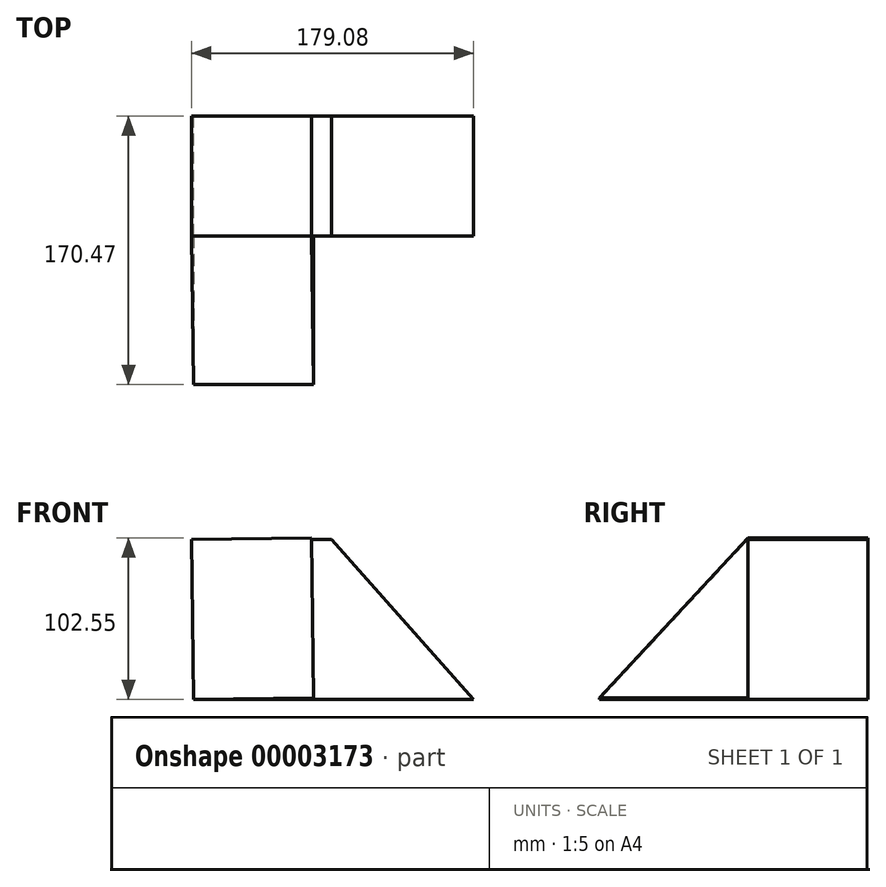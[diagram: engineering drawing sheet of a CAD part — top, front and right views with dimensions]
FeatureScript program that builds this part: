
annotation { "Feature Type Name" : "Feature", "Feature Type Description" : "" }
export const myFeature = defineFeature(function(context is Context, id is Id, definition is map)
    precondition{}
    {
        {
            var Q0;
            Q0=qCreatedBy(makeId("Front.planeOp"),FACE);
            var sketch = newSketch(context, id + "F0", { "sketchPlane" : qUnion([Q0])});
            skLineSegment(sketch, "E0.rect.bottom", {"start": v(-0.64, 50.8) * mm, "end": v(-89.54, 50.8) * mm});
            skLineSegment(sketch, "E0.rect.top", {"start": v(89.54, -50.8) * mm, "end": v(-88.26, -50.8) * mm});
            skLineSegment(sketch, "E0.rect.right", {"start": v(-89.54, 50.8) * mm, "end": v(-88.26, -50.8) * mm});
            skPoint(sketch, "E0.rect.middle", {"position": v(0, 0) * mm});
            skLineSegment(sketch, "E1", {"start": v(-0.64, 50.8) * mm, "end": v(89.54, -50.8) * mm});
            skPoint(sketch, "E2.orphan", {"position": v(88.26, 50.8) * mm});
            skSolve(sketch);
        }
        {
            var Q0;
            Q0=makeQuery(id+"F0.imprint","IMPRINT",FACE,{"disambiguationData":[TD([[makeQuery(id+"F0.imprint","IMPRINT",EDGE,{"derivedFrom":sQuery(id+"F0.wireOp",EDGE,"E0.rect.bottom")}),1.0]])]});
            extrude(context, id + "F1", {"entities" : qUnion([Q0]), "depth" : 76.2 * mm});
        }
        {
            var Q0;
            Q0=makeQuery(id+"F1.opExtrude","SWEPT_FACE",FACE,{"disambiguationData":[OSD([sQuery(id+"F0.wireOp",EDGE,"E0.rect.right")])]});
            var sketch = newSketch(context, id + "F2", { "sketchPlane" : qUnion([Q0])});
            skLineSegment(sketch, "E3", {"start": v(0, -49.68) * mm, "end": v(170.47, -49.68) * mm});
            skLineSegment(sketch, "E4", {"start": v(170.47, -49.68) * mm, "end": v(76.2, 51.92) * mm});
            skLineSegment(sketch, "E5", {"start": v(76.2, 51.92) * mm, "end": v(0, 51.92) * mm});
            skLineSegment(sketch, "E6", {"start": v(0, 51.92) * mm, "end": v(0, -49.68) * mm});
            skSolve(sketch);
        }
        {
            var Q0;
            Q0 = qSketchRegion(id + "F2", true);
            extrude(context, id + "F3", {"entities" : qUnion([Q0]), "operationType" : NewBodyOperationType.ADD, "oppositeDirection" : true, "depth" : 76.2 * mm});
        }
    });
